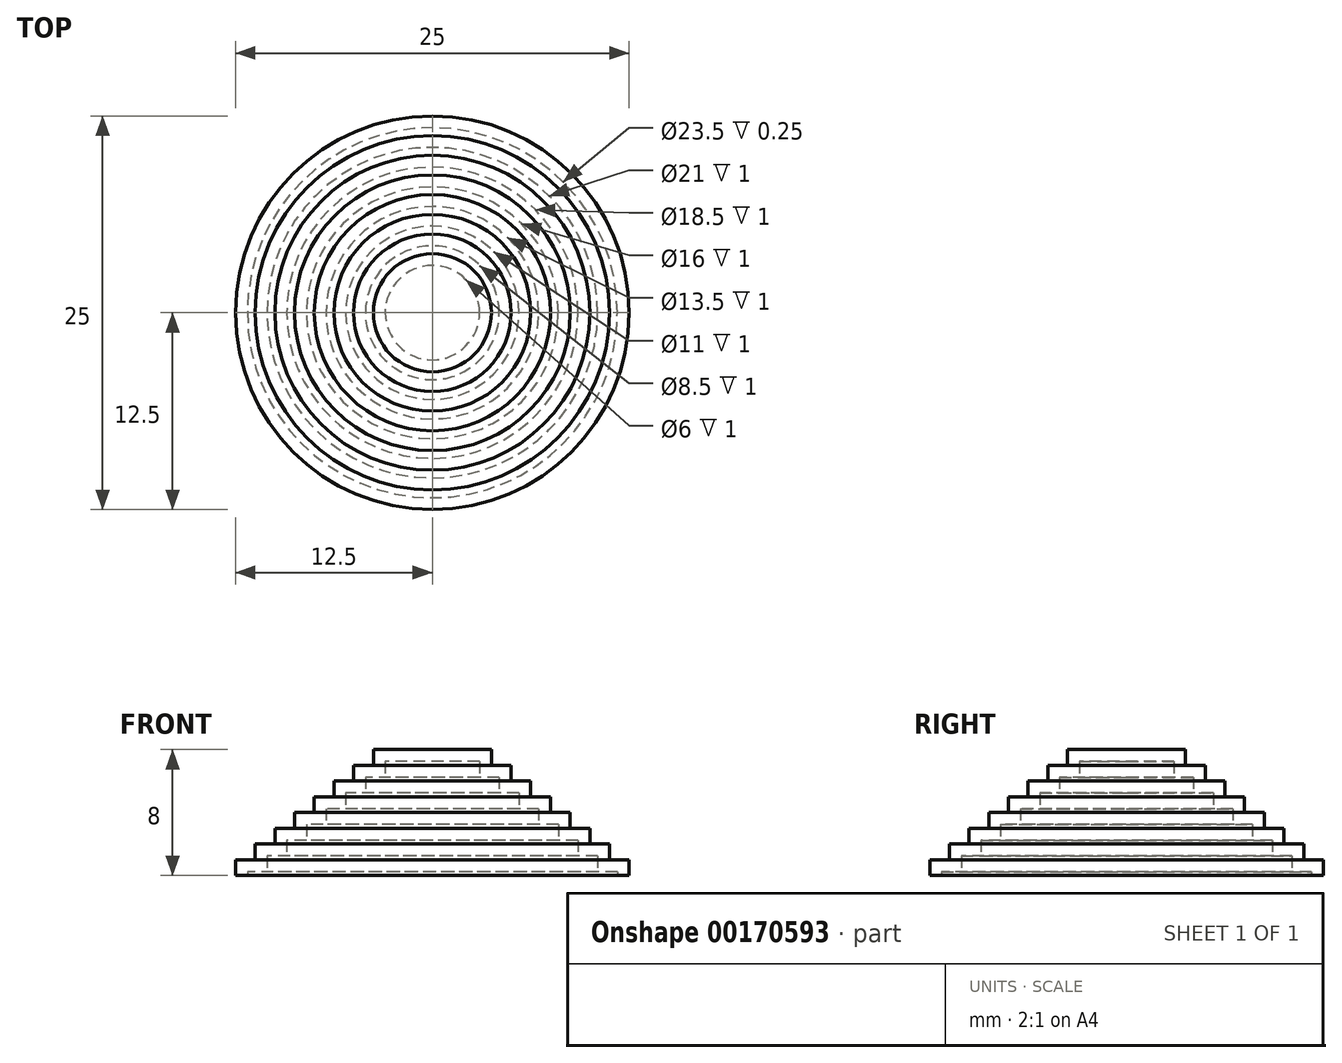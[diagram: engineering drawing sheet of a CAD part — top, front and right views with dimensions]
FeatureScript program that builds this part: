
annotation { "Feature Type Name" : "Feature", "Feature Type Description" : "" }
export const myFeature = defineFeature(function(context is Context, id is Id, definition is map)
    precondition{}
    {
        {
            var Q0;
            Q0=qCreatedBy(makeId("Top.planeOp"),FACE);
            var sketch = newSketch(context, id + "F0", { "sketchPlane" : qUnion([Q0])});
            skCircle(sketch, "E0", {"center": v(0, 0) * mm, "radius": 12.5 * mm});
            skSolve(sketch);
        }
        {
            var Q0;
            Q0=makeQuery(id+"F0.imprint","IMPRINT",FACE,{"disambiguationData":[TD([[makeQuery(id+"F0.imprint","IMPRINT",EDGE,{"derivedFrom":sQuery(id+"F0.wireOp",EDGE,"E0")}),1.0]])]});
            extrude(context, id + "F1", {"entities" : qUnion([Q0]), "depth" : 1 * mm});
        }
        {
            var Q0;
            Q0=makeQuery(id+"F1.opExtrude","CAP_FACE",FACE,{"disambiguationData":[OSD([sQuery(id+"F0.wireOp",EDGE,"E0")])],"isStart":false});
            var sketch = newSketch(context, id + "F2", { "sketchPlane" : qUnion([Q0])});
            skCircle(sketch, "E1", {"center": v(0, 0) * mm, "radius": 11.25 * mm});
            skSolve(sketch);
        }
        {
            var Q0;
            Q0=makeQuery(id+"F2.imprint","IMPRINT",FACE,{"disambiguationData":[TD([[makeQuery(id+"F2.imprint","IMPRINT",EDGE,{"derivedFrom":sQuery(id+"F2.wireOp",EDGE,"E1")}),1.0]])]});
            extrude(context, id + "F3", {"entities" : qUnion([Q0]), "operationType" : NewBodyOperationType.ADD, "depth" : 1 * mm});
        }
        {
            var Q0;
            Q0=makeQuery(id+"F3.opExtrude","CAP_FACE",FACE,{"disambiguationData":[OSD([sQuery(id+"F2.wireOp",EDGE,"E1")])],"isStart":false});
            var sketch = newSketch(context, id + "F4", { "sketchPlane" : qUnion([Q0])});
            skCircle(sketch, "E2", {"center": v(0, 0) * mm, "radius": 10 * mm});
            skSolve(sketch);
        }
        {
            var Q0;
            Q0=makeQuery(id+"F4.imprint","IMPRINT",FACE,{"disambiguationData":[TD([[makeQuery(id+"F4.imprint","IMPRINT",EDGE,{"derivedFrom":sQuery(id+"F4.wireOp",EDGE,"E2")}),1.0]])]});
            extrude(context, id + "F5", {"entities" : qUnion([Q0]), "operationType" : NewBodyOperationType.ADD, "depth" : 1 * mm});
        }
        {
            var Q0;
            Q0=makeQuery(id+"F5.opExtrude","CAP_FACE",FACE,{"disambiguationData":[OSD([sQuery(id+"F4.wireOp",EDGE,"E2")])],"isStart":false});
            var sketch = newSketch(context, id + "F6", { "sketchPlane" : qUnion([Q0])});
            skCircle(sketch, "E3", {"center": v(0, 0) * mm, "radius": 8.75 * mm});
            skSolve(sketch);
        }
        {
            var Q0;
            Q0=makeQuery(id+"F6.imprint","IMPRINT",FACE,{"disambiguationData":[TD([[makeQuery(id+"F6.imprint","IMPRINT",EDGE,{"derivedFrom":sQuery(id+"F6.wireOp",EDGE,"E3")}),1.0]])]});
            extrude(context, id + "F7", {"entities" : qUnion([Q0]), "operationType" : NewBodyOperationType.ADD, "depth" : 1 * mm});
        }
        {
            var Q0;
            Q0=makeQuery(id+"F7.opExtrude","CAP_FACE",FACE,{"disambiguationData":[OSD([sQuery(id+"F6.wireOp",EDGE,"E3")])],"isStart":false});
            var sketch = newSketch(context, id + "F8", { "sketchPlane" : qUnion([Q0])});
            skCircle(sketch, "E4", {"center": v(0, 0) * mm, "radius": 7.5 * mm});
            skSolve(sketch);
        }
        {
            var Q0;
            Q0=makeQuery(id+"F8.imprint","IMPRINT",FACE,{"disambiguationData":[TD([[makeQuery(id+"F8.imprint","IMPRINT",EDGE,{"derivedFrom":sQuery(id+"F8.wireOp",EDGE,"E4")}),1.0]])]});
            extrude(context, id + "F9", {"entities" : qUnion([Q0]), "operationType" : NewBodyOperationType.ADD, "depth" : 1 * mm});
        }
        {
            var Q0;
            Q0=makeQuery(id+"F9.opExtrude","CAP_FACE",FACE,{"disambiguationData":[OSD([sQuery(id+"F8.wireOp",EDGE,"E4")])],"isStart":false});
            var sketch = newSketch(context, id + "F10", { "sketchPlane" : qUnion([Q0])});
            skCircle(sketch, "E5", {"center": v(0, 0) * mm, "radius": 6.25 * mm});
            skSolve(sketch);
        }
        {
            var Q0;
            Q0=makeQuery(id+"F10.imprint","IMPRINT",FACE,{"disambiguationData":[TD([[makeQuery(id+"F10.imprint","IMPRINT",EDGE,{"derivedFrom":sQuery(id+"F10.wireOp",EDGE,"E5")}),1.0]])]});
            extrude(context, id + "F11", {"entities" : qUnion([Q0]), "operationType" : NewBodyOperationType.ADD, "depth" : 1 * mm});
        }
        {
            var Q0;
            Q0=makeQuery(id+"F11.opExtrude","CAP_FACE",FACE,{"disambiguationData":[OSD([sQuery(id+"F10.wireOp",EDGE,"E5")])],"isStart":false});
            var sketch = newSketch(context, id + "F12", { "sketchPlane" : qUnion([Q0])});
            skCircle(sketch, "E6", {"center": v(0, 0) * mm, "radius": 5 * mm});
            skSolve(sketch);
        }
        {
            var Q0;
            Q0=makeQuery(id+"F12.imprint","IMPRINT",FACE,{"disambiguationData":[TD([[makeQuery(id+"F12.imprint","IMPRINT",EDGE,{"derivedFrom":sQuery(id+"F12.wireOp",EDGE,"E6")}),1.0]])]});
            extrude(context, id + "F13", {"entities" : qUnion([Q0]), "operationType" : NewBodyOperationType.ADD, "depth" : 1 * mm});
        }
        {
            var Q0;
            Q0=makeQuery(id+"F13.opExtrude","CAP_FACE",FACE,{"disambiguationData":[OSD([sQuery(id+"F12.wireOp",EDGE,"E6")])],"isStart":false});
            var sketch = newSketch(context, id + "F14", { "sketchPlane" : qUnion([Q0])});
            skCircle(sketch, "E7", {"center": v(0, 0) * mm, "radius": 3.75 * mm});
            skSolve(sketch);
        }
        {
            var Q0;
            Q0=makeQuery(id+"F14.imprint","IMPRINT",FACE,{"disambiguationData":[TD([[makeQuery(id+"F14.imprint","IMPRINT",EDGE,{"derivedFrom":sQuery(id+"F14.wireOp",EDGE,"E7")}),1.0]])]});
            var Q1;
            Q1=sQuery(id+"F14.wireOp",EDGE,"E7");
            extrude(context, id + "F15", {"entities" : qUnion([Q0]), "operationType" : NewBodyOperationType.ADD, "surfaceEntities" : qUnion([Q1]), "depth" : 1 * mm});
        }
        {
            var Q0;
            Q0=makeQuery(id+"F1.opExtrude","CAP_FACE",FACE,{"disambiguationData":[OSD([sQuery(id+"F0.wireOp",EDGE,"E0")])],"isStart":true});
            shell(context, id + "F16", {"entities" : qUnion([Q0]), "thickness" : 0.75 * mm});
        }
    });
